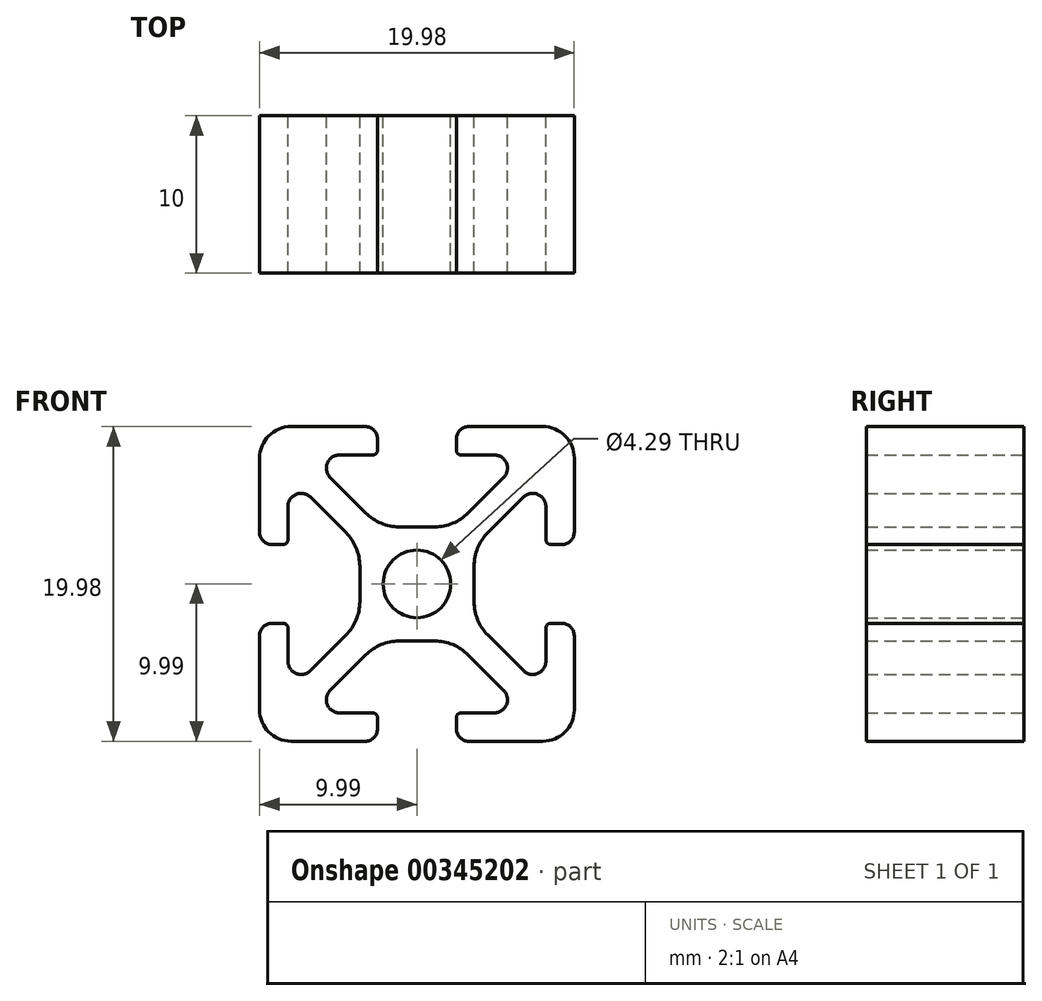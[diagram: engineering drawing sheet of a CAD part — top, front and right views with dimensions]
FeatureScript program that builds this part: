
annotation { "Feature Type Name" : "Feature", "Feature Type Description" : "" }
export const myFeature = defineFeature(function(context is Context, id is Id, definition is map)
    precondition{}
    {
        {
            var Q0;
            Q0=qCreatedBy(makeId("Front.planeOp"),FACE);
            var sketch = newSketch(context, id + "F0", { "sketchPlane" : qUnion([Q0])});
            skLineSegment(sketch, "E0", {"start": v(-7.99, 10) * mm, "end": v(-3.29, 10) * mm});
            skArc(sketch, "E1", {"start": v(-3.29, 10) * mm, "mid": v(-2.73, 9.76) * mm, "end": v(-2.5, 9.2) * mm});
            skLineSegment(sketch, "E2", {"start": v(-2.5, 9.2) * mm, "end": v(-2.5, 8.5) * mm});
            skLineSegment(sketch, "E3", {"start": v(-5.5, 6.76) * mm, "end": v(-3.25, 4.5) * mm});
            skArc(sketch, "E4", {"start": v(-4.91, 8.2) * mm, "mid": v(-5.69, 7.67) * mm, "end": v(-5.5, 6.76) * mm});
            skLineSegment(sketch, "E5", {"start": v(3.29, 10) * mm, "end": v(7.99, 10) * mm});
            skArc(sketch, "E6", {"start": v(2.5, 9.2) * mm, "mid": v(2.73, 9.76) * mm, "end": v(3.29, 10) * mm});
            skLineSegment(sketch, "E7", {"start": v(3.25, 4.5) * mm, "end": v(5.5, 6.76) * mm});
            skArc(sketch, "E8", {"start": v(1.13, 3.63) * mm, "mid": v(2.28, 3.86) * mm, "end": v(3.25, 4.5) * mm});
            skArc(sketch, "E9", {"start": v(7.99, 10) * mm, "mid": v(9.4, 9.4) * mm, "end": v(10, 7.99) * mm});
            skLineSegment(sketch, "E10", {"start": v(-2.8, 8.2) * mm, "end": v(-4.91, 8.2) * mm});
            skArc(sketch, "E11", {"start": v(-2.5, 8.5) * mm, "mid": v(-2.6, 8.28) * mm, "end": v(-2.8, 8.2) * mm});
            skLineSegment(sketch, "E12", {"start": v(4.91, 8.2) * mm, "end": v(2.8, 8.2) * mm});
            skLineSegment(sketch, "E13", {"start": v(2.5, 8.5) * mm, "end": v(2.5, 9.2) * mm});
            skArc(sketch, "E14", {"start": v(2.8, 8.2) * mm, "mid": v(2.6, 8.28) * mm, "end": v(2.5, 8.5) * mm});
            skArc(sketch, "E15", {"start": v(5.5, 6.76) * mm, "mid": v(5.69, 7.67) * mm, "end": v(4.91, 8.2) * mm});
            skLineSegment(sketch, "E16", {"start": v(-1.13, 3.63) * mm, "end": v(1.13, 3.63) * mm});
            skArc(sketch, "E17", {"start": v(-3.25, 4.5) * mm, "mid": v(-2.28, 3.86) * mm, "end": v(-1.13, 3.63) * mm});
            skArc(sketch, "E18", {"start": v(-10, 7.99) * mm, "mid": v(-9.4, 9.4) * mm, "end": v(-7.99, 10) * mm});
            skLineSegment(sketch, "E19", {"start": v(10, 7.99) * mm, "end": v(10, 3.29) * mm});
            skLineSegment(sketch, "E20", {"start": v(4.5, -3.25) * mm, "end": v(6.76, -5.5) * mm});
            skArc(sketch, "E21", {"start": v(3.63, -1.13) * mm, "mid": v(3.86, -2.28) * mm, "end": v(4.5, -3.25) * mm});
            skLineSegment(sketch, "E22", {"start": v(3.63, 1.13) * mm, "end": v(3.63, -1.13) * mm});
            skArc(sketch, "E23", {"start": v(9.2, -2.5) * mm, "mid": v(9.76, -2.73) * mm, "end": v(10, -3.29) * mm});
            skLineSegment(sketch, "E24", {"start": v(10, -3.29) * mm, "end": v(10, -7.99) * mm});
            skLineSegment(sketch, "E25", {"start": v(8.5, -2.5) * mm, "end": v(9.2, -2.5) * mm});
            skLineSegment(sketch, "E26", {"start": v(-9.2, -2.5) * mm, "end": v(-8.5, -2.5) * mm});
            skArc(sketch, "E27", {"start": v(-10, -3.29) * mm, "mid": v(-9.76, -2.73) * mm, "end": v(-9.2, -2.5) * mm});
            skLineSegment(sketch, "E28", {"start": v(-8.2, -2.8) * mm, "end": v(-8.2, -4.91) * mm});
            skLineSegment(sketch, "E29", {"start": v(-10, 3.29) * mm, "end": v(-10, 7.99) * mm});
            skArc(sketch, "E30", {"start": v(-9.2, 2.5) * mm, "mid": v(-9.76, 2.73) * mm, "end": v(-10, 3.29) * mm});
            skLineSegment(sketch, "E31", {"start": v(-4.5, 3.25) * mm, "end": v(-6.76, 5.5) * mm});
            skLineSegment(sketch, "E32", {"start": v(-3.63, -1.13) * mm, "end": v(-3.63, 1.13) * mm});
            skArc(sketch, "E33", {"start": v(-3.63, 1.13) * mm, "mid": v(-3.86, 2.28) * mm, "end": v(-4.5, 3.25) * mm});
            skArc(sketch, "E34", {"start": v(-6.76, 5.5) * mm, "mid": v(-7.67, 5.69) * mm, "end": v(-8.2, 4.91) * mm});
            skLineSegment(sketch, "E35", {"start": v(-8.5, 2.5) * mm, "end": v(-9.2, 2.5) * mm});
            skLineSegment(sketch, "E36", {"start": v(8.2, 2.8) * mm, "end": v(8.2, 4.91) * mm});
            skArc(sketch, "E37", {"start": v(8.2, 4.91) * mm, "mid": v(7.67, 5.69) * mm, "end": v(6.76, 5.5) * mm});
            skLineSegment(sketch, "E38", {"start": v(-10, -7.99) * mm, "end": v(-10, -3.29) * mm});
            skArc(sketch, "E39", {"start": v(-4.5, -3.25) * mm, "mid": v(-3.86, -2.28) * mm, "end": v(-3.63, -1.13) * mm});
            skLineSegment(sketch, "E40", {"start": v(-6.76, -5.5) * mm, "end": v(-4.5, -3.25) * mm});
            skLineSegment(sketch, "E41", {"start": v(1.13, -3.63) * mm, "end": v(-1.13, -3.63) * mm});
            skLineSegment(sketch, "E42", {"start": v(5.5, -6.76) * mm, "end": v(3.25, -4.5) * mm});
            skArc(sketch, "E43", {"start": v(3.25, -4.5) * mm, "mid": v(2.28, -3.86) * mm, "end": v(1.13, -3.63) * mm});
            skLineSegment(sketch, "E44", {"start": v(8.2, -4.91) * mm, "end": v(8.2, -2.8) * mm});
            skLineSegment(sketch, "E45", {"start": v(-4.91, -8.2) * mm, "end": v(-2.8, -8.2) * mm});
            skArc(sketch, "E46", {"start": v(-5.5, -6.76) * mm, "mid": v(-5.69, -7.67) * mm, "end": v(-4.91, -8.2) * mm});
            skArc(sketch, "E47", {"start": v(-8.2, -4.91) * mm, "mid": v(-7.67, -5.69) * mm, "end": v(-6.76, -5.5) * mm});
            skArc(sketch, "E48", {"start": v(-8.5, -2.5) * mm, "mid": v(-8.28, -2.6) * mm, "end": v(-8.2, -2.8) * mm});
            skArc(sketch, "E49", {"start": v(4.91, -8.2) * mm, "mid": v(5.69, -7.67) * mm, "end": v(5.5, -6.76) * mm});
            skLineSegment(sketch, "E50", {"start": v(2.5, -9.2) * mm, "end": v(2.5, -8.5) * mm});
            skArc(sketch, "E51", {"start": v(2.5, -8.5) * mm, "mid": v(2.6, -8.28) * mm, "end": v(2.8, -8.2) * mm});
            skLineSegment(sketch, "E52", {"start": v(2.8, -8.2) * mm, "end": v(4.91, -8.2) * mm});
            skArc(sketch, "E53", {"start": v(3.29, -10) * mm, "mid": v(2.73, -9.76) * mm, "end": v(2.5, -9.2) * mm});
            skArc(sketch, "E54", {"start": v(6.76, -5.5) * mm, "mid": v(7.67, -5.69) * mm, "end": v(8.2, -4.91) * mm});
            skArc(sketch, "E55", {"start": v(10, -7.99) * mm, "mid": v(9.4, -9.4) * mm, "end": v(7.99, -10) * mm});
            skArc(sketch, "E56", {"start": v(4.5, 3.25) * mm, "mid": v(3.86, 2.28) * mm, "end": v(3.63, 1.13) * mm});
            skLineSegment(sketch, "E57", {"start": v(-3.25, -4.5) * mm, "end": v(-5.5, -6.76) * mm});
            skLineSegment(sketch, "E58", {"start": v(-2.5, -8.5) * mm, "end": v(-2.5, -9.2) * mm});
            skArc(sketch, "E59", {"start": v(-2.8, -8.2) * mm, "mid": v(-2.6, -8.28) * mm, "end": v(-2.5, -8.5) * mm});
            skArc(sketch, "E60", {"start": v(-2.5, -9.2) * mm, "mid": v(-2.73, -9.76) * mm, "end": v(-3.29, -10) * mm});
            skArc(sketch, "E61", {"start": v(-1.13, -3.63) * mm, "mid": v(-2.28, -3.86) * mm, "end": v(-3.25, -4.5) * mm});
            skArc(sketch, "E62", {"start": v(10, 3.29) * mm, "mid": v(9.76, 2.73) * mm, "end": v(9.2, 2.5) * mm});
            skLineSegment(sketch, "E63", {"start": v(6.76, 5.5) * mm, "end": v(4.5, 3.25) * mm});
            skLineSegment(sketch, "E64", {"start": v(-8.2, 4.91) * mm, "end": v(-8.2, 2.8) * mm});
            skLineSegment(sketch, "E65", {"start": v(-3.29, -10) * mm, "end": v(-7.99, -10) * mm});
            skArc(sketch, "E66", {"start": v(-7.99, -10) * mm, "mid": v(-9.4, -9.4) * mm, "end": v(-10, -7.99) * mm});
            skLineSegment(sketch, "E67", {"start": v(7.99, -10) * mm, "end": v(3.29, -10) * mm});
            skLineSegment(sketch, "E68", {"start": v(9.2, 2.5) * mm, "end": v(8.5, 2.5) * mm});
            skArc(sketch, "E69", {"start": v(8.5, 2.5) * mm, "mid": v(8.28, 2.6) * mm, "end": v(8.2, 2.8) * mm});
            skCircle(sketch, "E70", {"center": v(0, 0) * mm, "radius": 2.15 * mm});
            skArc(sketch, "E71", {"start": v(-8.2, 2.8) * mm, "mid": v(-8.28, 2.6) * mm, "end": v(-8.5, 2.5) * mm});
            skArc(sketch, "E72", {"start": v(8.2, -2.8) * mm, "mid": v(8.28, -2.6) * mm, "end": v(8.5, -2.5) * mm});
            skSolve(sketch);
        }
        {
            var Q0;
            Q0=qSketchRegion(id+"F0",true);
            extrude(context, id + "F1", {"entities" : qUnion([Q0]), "depth" : 10 * mm});
        }
    });
